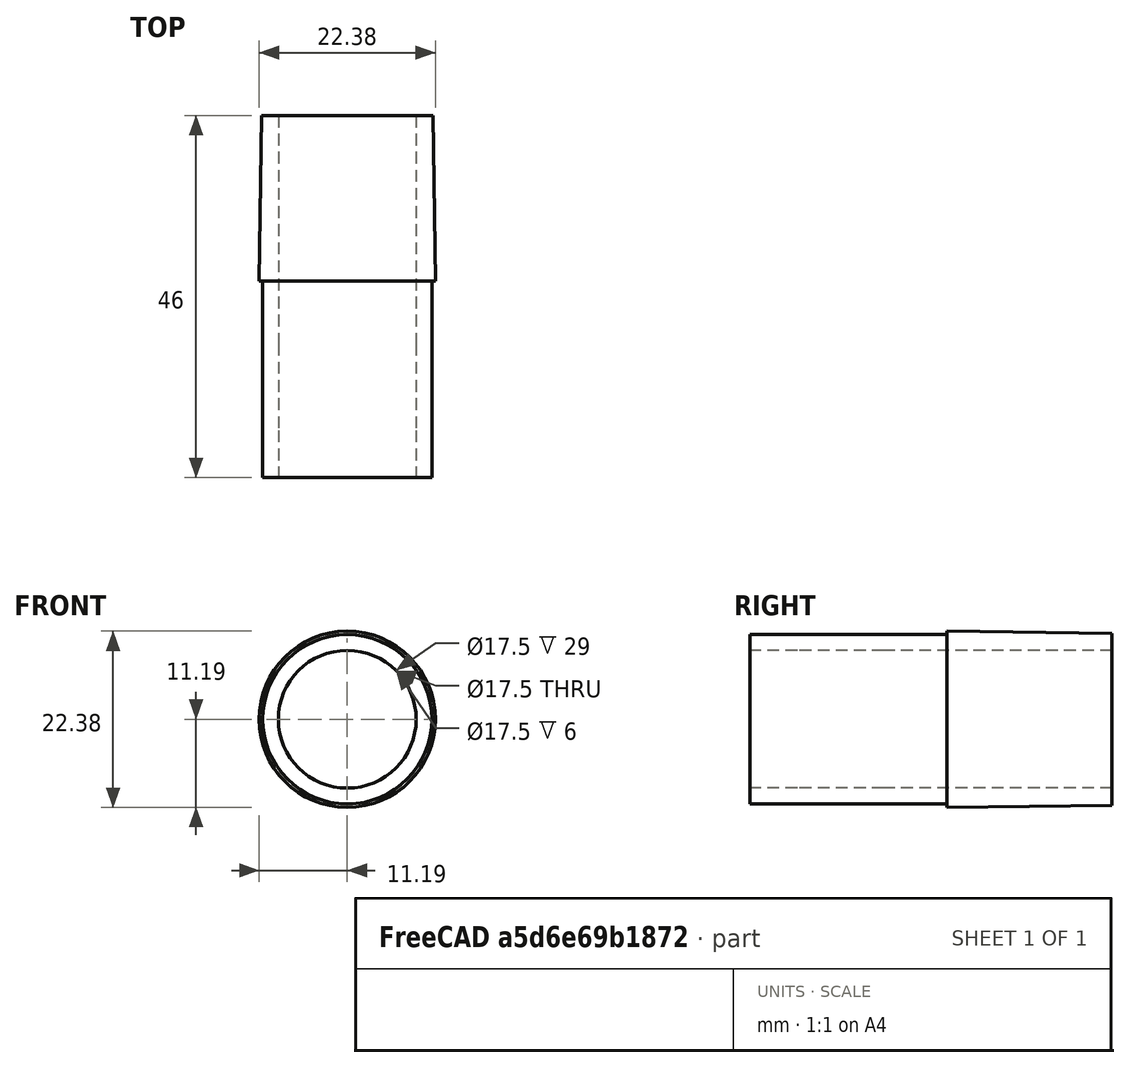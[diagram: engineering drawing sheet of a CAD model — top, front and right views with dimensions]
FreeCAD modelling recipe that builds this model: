
FCSTD DOCUMENT  (FreeCAD 0.18R4 (GitTag))
Label: BlowerOutletAdapter-V1
License: All rights reserved
LicenseURL: http://en.wikipedia.org/wiki/All_rights_reserved
objects: Part::Cylinder×3, Part::MultiFuse×2, Part::Cone×1, Part::Cut×1
note: 7 computed .brp shape members not serialized (recipe doc carries the construction recipe); baked Part::Feature solids carry a one-line shape summary decoded from their .brp

FEATURE [Part::Cone] Cone001  label="22mmTaper"
  Angle = 360
  AttacherType = Attacher::AttachEngine3D
  Height = 21
  Placement = pos=(20,65.3,13.5) rot=(0,0.707107,-0.707107;3.14159rad)
  Radius1 = 10.92
  Radius2 = 11.19
FEATURE [Part::Cylinder] Cylinder005  label="OutletExtension"
  Angle = 360
  AttacherType = Attacher::AttachEngine3D
  Height = 40
  Placement = pos=(20,65.3,13.5) rot=(1,0,0;1.5708rad)
  Radius = 8.75
FEATURE [Part::Cylinder] Cylinder007  label="HousingOutlet"
  Angle = 360
  AttacherType = Attacher::AttachEngine3D
  Height = 40
  Placement = pos=(20,59.3,13.5) rot=(1,0,0;1.5708rad)
  Radius = 10.75
FEATURE [Part::Cylinder] Cylinder003  label="BlowerOutlet"
  Angle = 360
  AttacherType = Attacher::AttachEngine3D
  Height = 40
  Placement = pos=(20,36.3,13.5) rot=(1,0,0;1.5708rad)
  Radius = 8.75
FEATURE [Part::MultiFuse] Fusion  label="Outside"
  Shapes = -> [Cone001,Cylinder007]
FEATURE [Part::MultiFuse] Fusion001  label="inside"
  Shapes = -> [Cylinder003,Cylinder005]
FEATURE [Part::Cut] Cut  label="BlowerOutletAdapter"
  Base = -> Fusion
  Tool = -> Fusion001
